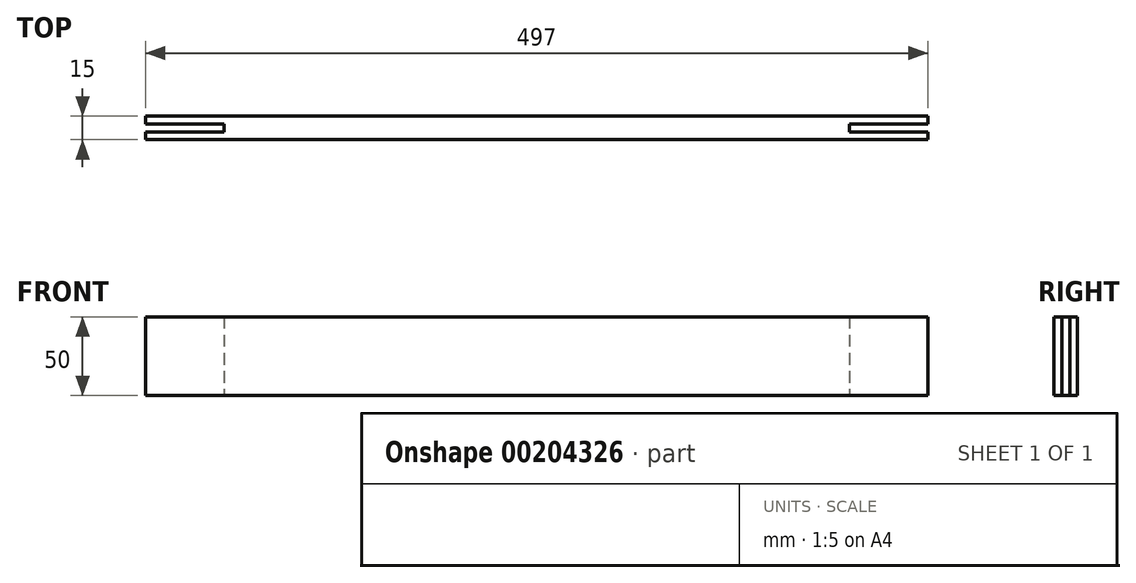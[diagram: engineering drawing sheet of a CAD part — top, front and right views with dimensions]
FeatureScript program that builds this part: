
annotation { "Feature Type Name" : "Feature", "Feature Type Description" : "" }
export const myFeature = defineFeature(function(context is Context, id is Id, definition is map)
    precondition{}
    {
        {
            var Q0;
            Q0=qCreatedBy(makeId("Top.planeOp"),FACE);
            var sketch = newSketch(context, id + "F0", { "sketchPlane" : qUnion([Q0])});
            skLineSegment(sketch, "E0.bottom", {"start": v(0, 0) * mm, "end": v(497, 0) * mm});
            skLineSegment(sketch, "E0.top", {"start": v(0, 15) * mm, "end": v(497, 15) * mm});
            skLineSegment(sketch, "E1", {"start": v(0, 10) * mm, "end": v(50, 10) * mm});
            skLineSegment(sketch, "E2", {"start": v(50, 10) * mm, "end": v(50, 5) * mm});
            skLineSegment(sketch, "E3", {"start": v(50, 5) * mm, "end": v(0, 5) * mm});
            skLineSegment(sketch, "E4", {"start": v(248.5, 0) * mm, "end": v(248.5, -22.06) * mm, "construction": true});
            skLineSegment(sketch, "E5.MirrorCS", {"start": v(497, 10) * mm, "end": v(447, 10) * mm});
            skLineSegment(sketch, "E6.MirrorCS", {"start": v(447, 10) * mm, "end": v(447, 5) * mm});
            skLineSegment(sketch, "E7.MirrorCS", {"start": v(447, 5) * mm, "end": v(497, 5) * mm});
            skLineSegment(sketch, "E8", {"start": v(0, 5) * mm, "end": v(0, 0) * mm});
            skLineSegment(sketch, "E9", {"start": v(0, 15) * mm, "end": v(0, 10) * mm});
            skLineSegment(sketch, "E10", {"start": v(497, 10) * mm, "end": v(497, 15) * mm});
            skLineSegment(sketch, "E11", {"start": v(497, 5) * mm, "end": v(497, 0) * mm});
            skSolve(sketch);
        }
        {
            var Q0;
            Q0 = qSketchRegion(id + "F0", true);
            extrude(context, id + "F1", {"entities" : qUnion([Q0]), "depth" : 50 * mm});
        }
    });
